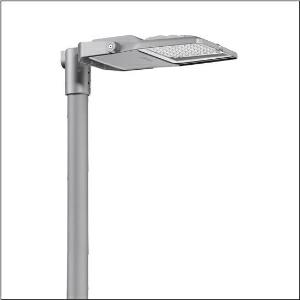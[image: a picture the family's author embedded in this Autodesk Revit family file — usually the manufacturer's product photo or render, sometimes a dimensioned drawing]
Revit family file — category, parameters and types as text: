
# Revit family: floodlight_fl_21_iq_mini___pl64_5xa7772d4e3a_9d14
name_source: partatom
category: Lighting Fixtures
units: mm (PartAtom-declared; Revit-internal decimal feet)

## family parameters
Cut with Voids When Loaded = No
Host = Face
Light Source = No
Part Type = Normal
Room Calculation Point = No
Round Connector Dimension = Use Diameter
Shared = No

## types (1)
- --- (1 x LED, 17970 lm, 143 W, 4000K)
    Apparent Load = 143 VA
    CIE Flux Codes = 28 80 98 100 100
    Color Rendering = 70
    Color Temperature = 4000K
    Default Elevation = 1800 mm
    Description = Floodlight FL 21 iQ mini, floodlight, primary light control with lens, of PMMA, primary optical cover: protective disc, of toughened safety glass, transparent, light distribution: PL64, light emission: direct distribution, installation type: surface-mounted, LED, High Power LED, rated luminous flux: 17.970lm, luminous efficacy: 126lm/W, light colour: 740, colour temperature: 4000K, control: Auto-Match, Temp-Guard, Night-Set, Smart-Wire, Desk-Remote (wireless, voltage-free reading and setting of iQ features in the workshop via application-optimized NFC function/RFID function), optimised constant luminous flux control (CLO 2.0), Light-Fading, Lumen-Switch, with terminal, 6-pole, mains connection: 220..240V, AC, 50/60Hz, start of lifetime: 143W, end of service life: 152W, reduction: 61W, luminaire housing, of diecast aluminium, powder-coated, Siteco® metallic grey (DB 702S), corrosivity category C5 mid according to DIN EN ISO 12944, sealing non-destructively replaceable, please order mast flange separately, mast bracket, of steel, galvanised, powder-coated, protection rating (complete): IP66, insulation class (complete): insulation class II (safety insulation), certification: CE, ENEC, VDE, protection symbol: D, impact resistance: IK08, permissible operating ambient temperature: -40..+40°C, permissible operating ambient temperature for outdoor applications: -40..+50°C, standard: DIN EN 12944, LABS conformity tested according to VDMA 24364:2018-05, packaging unit: 1 piece

Light Distribution: PL64
    Height = 70 mm
    Lamp = 1 x LED
    Lamp Light Flux = 17970 lm
    Lamp Power = 143 W
    Lamp count = 1
    Length = 485 mm
    Luminous efficacy = 126 lm/W
    Manufacturer = Siteco
    ModVariant = No
    Model = 5XA7772D4E3A
    Number of Poles = 1
    OnlyDefault = Yes
    Power Factor = 1
    Product Name = Floodlight FL 21 iQ mini | PL64
    Product group = floodlight | pylon annexe
    ProductGroupID = 6200
    Protection Class = Protection class II
    Protection Degree = IP 66
    RLX_Detail_Level = 1
    RLX_Emergency_Light_Flux = 0 lm
    RLX_Emergency_Type = 0
    RLX_Emergency_Type_DB = No
    RlxData = <blob elided: 101405 chars, md5=b5ce462c>
    Socket = socket
    Standby Power = 0 W
    System Light Flux = 17970 lm
    System Power = 143 W
    Type Comments = factory setting: luminous flux: 100 % | dim-lin: 254 | 730 mA
    Type Image = l_1007125.jpg
    URL = http://relux.com
    VarID = @adj_135983
    Voltage = 0 V
    Weight = 0.00 kg
    Width = 337 mm

## geometry (parser evidence)
native form markers: Blend x4, Sweep x11
no freeform markers — native parametric forms only
